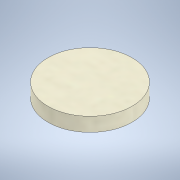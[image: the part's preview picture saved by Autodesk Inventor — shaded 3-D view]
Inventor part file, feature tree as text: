
AUTODESK INVENTOR PART (.ipt)
format: ipt  version: 2021 (Build 250183000, 183)  size: 99,840 bytes
history: native  units: mm
features: extrude x1, sketch x1
ambient origin geometry x8: Origin, YZ Plane, XZ Plane, XY Plane, X Axis, Y Axis, Z Axis, Center Point
bodies: Solid1 (feature_tree)
feature tree (2):
  extrude  "Extrusion1"  Depth=5.25mm TaperAngle=0.0deg
  sketch  "Sketch1"  dims[d0=31.7mm d1=5.25mm d2=0.0mm]
